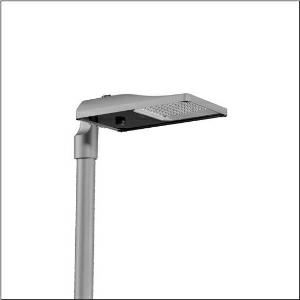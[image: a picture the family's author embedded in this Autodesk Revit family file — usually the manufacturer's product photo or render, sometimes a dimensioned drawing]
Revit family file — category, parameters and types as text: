
# Revit family: streetlight_sl_31_midi___pl52_5xh7h31t08ma_deac
name_source: partatom
category: Lighting Fixtures
units: mm (PartAtom-declared; Revit-internal decimal feet)

## family parameters
Cut with Voids When Loaded = No
Host = Face
Light Source = No
Part Type = Normal
Room Calculation Point = No
Round Connector Dimension = Use Diameter
Shared = No

## types (1)
- --- (1 x LED, 18970 lm, 142.8 W, 3000K)
    Apparent Load = 143 VA
    CIE Flux Codes = 27 59 98 100 100
    Color Rendering = 70
    Color Temperature = 3000K
    Default Elevation = 1800 mm
    Description = Streetlight SL 31 midi D4i, Desk-Remote mast luminaire for post-top, side-entry; light control with lens of PMMA; light distribution: PL52, direct asymmetric distribution, for standard-compliant lighting for roads and squares; LED: luminous flux: 18.970lm, light colour: 730, colour temperature: 3000K; luminous efficacy: 132,8lm/W; control: pre-setting: logarithmic dimming characteristic, flexible luminous flux parameterisation, time-dependent luminous flux control, constant luminous flux control, power reduction, intelligent temperature release in ECG and LED module, overheat protection; luminaire housing, of diecast aluminium, Siteco® metallic grey (DB 702S), corrosivity category C5 high according to DIN EN ISO 12944; cover of toughened safety glass, transparent, opened without tools; mast flange of diecast aluminium, Siteco® metallic grey (DB 702S), spigot size: 76/60mm, mast flange included unmounted; with cable H07RN-F 2x 1.5mm², cable length: 12,5m, connection cable pre-assembled; mains connection: 220..240V, AC, 50/60Hz; power consumption (at start of service life): 142,8W / (at end of service life): 158,8W / (with reduced operation 50%): 60W; protection rating (complete): IP66; insulation class (complete): insulation class II (safety insulation); impact resistance: IK09; certification: CE, ENEC, ENEC+, VDE, UKCA, ZD4i; permissible operating ambient temperature for outdoor applications: -40..+50°C; packaging unit: 1 piece

Light Distribution: PL52
    Height = 79 mm
    Lamp = 1 x LED
    Lamp Light Flux = 18970 lm
    Lamp Power = 142.8 W
    Lamp count = 1
    Length = 577 mm
    Luminous efficacy = 133 lm/W
    Manufacturer = Siteco
    ModVariant = No
    Model = 5XH7H31T08MA
    Number of Poles = 1
    OnlyDefault = Yes
    Power Factor = 1
    Product Name = Streetlight SL 31 midi | PL52
    Product group = mast luminaire | pylon top
    ProductGroupID = 6100
    Protection Class = Protection class II
    Protection Degree = IP 66
    RLX_Detail_Level = 1
    RLX_Emergency_Light_Flux = 0 lm
    RLX_Emergency_Type = 0
    RLX_Emergency_Type_DB = No
    RlxData = <blob elided: 52609 chars, md5=1d6942aa>
    Socket = socket
    Standby Power = 0 W
    System Light Flux = 18970 lm
    System Power = 143 W
    Type Comments = factory setting: luminous flux: 100 % | dim-lin: 254 | 735 mA
    Type Image = l_1300321.jpg
    URL = http://relux.com
    VarID = @adj_077879
    Voltage = 0 V
    Weight = 0.00 kg
    Width = 362 mm

## geometry (parser evidence)
native form markers: Blend x4, Sweep x10
no freeform markers — native parametric forms only
